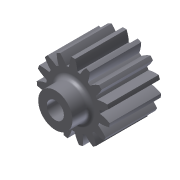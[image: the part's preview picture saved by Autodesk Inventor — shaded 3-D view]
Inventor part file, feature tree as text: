
AUTODESK INVENTOR PART (.ipt)
format: ipt  version: 2011 (Build 150239000, 239)  size: 229,376 bytes
history: native  units: mm (DEFAULTED — no unit token found)
features: other x4, sketch x4, extrude x3, plane x3, fillet x1
ambient origin geometry x8: Origin, YZ Plane, XZ Plane, XY Plane, X Axis, Y Axis, Z Axis, Center Point
bodies: Solid1 (feature_tree)
feature tree (15):
  other  "Gear 15T 32dp 125press"
  extrude  "Extrusion1"  Depth=9.525mm TaperAngle=0.0deg
  plane  "Work Plane1"
  plane  "Work Plane2"
  plane  "Work Plane3"
  other  "Spur Gear"
  extrude  "Extrusion2"  Depth=76.2mm TaperAngle=0.0deg
  extrude  "Extrusion3"  TaperAngle=0.0deg  [1 undecoded]
  fillet  "Fillet1"  Radius=11.90625mm
  sketch  "Sketch1"  dims[d0=13.49375mm d1=9.525mm d2=0.0mm]
  sketch  "Sketch2"  dims[d3=11.90625mm d4=76.2mm d5=0.0mm]
  other  "Srf1"
  sketch  "Sketch3"  dims[d6=0.0mm d7=2.094395mm d9=0.0mm d14=0.0mm d15=11.90625mm]
  sketch  "Sketch4"  dims[d16=0.0mm d17=0.0mm d18=0.0mm d19=11.90625mm d20=6.35mm d21=3.302mm d22=0.0mm d23=3.175mm d24=3.302mm d25=0.0mm d26=0.79375mm]
  other  "Pitch Diameter"
note: 1 required parameter value undecoded (feature->parameter linkage not recoverable at this tier; creation-order binding heuristic only, values carry confidence <= 0.55)
